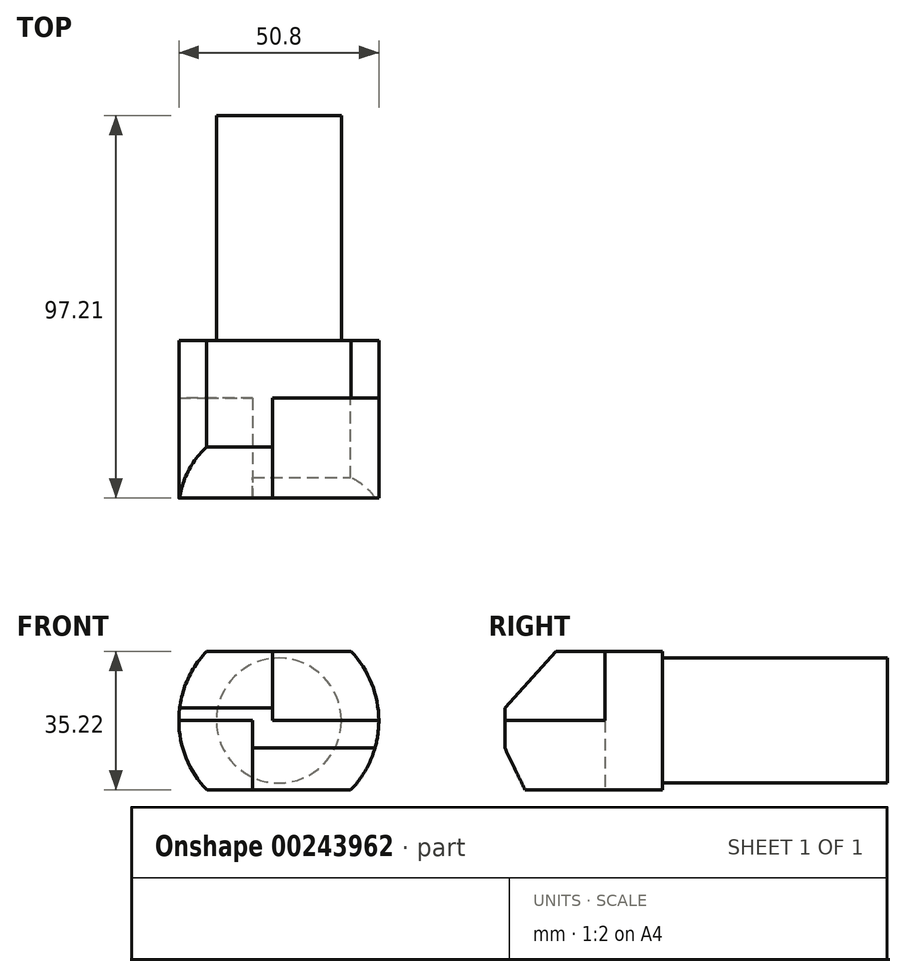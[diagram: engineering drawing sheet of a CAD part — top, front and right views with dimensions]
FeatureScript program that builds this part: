
annotation { "Feature Type Name" : "Feature", "Feature Type Description" : "" }
export const myFeature = defineFeature(function(context is Context, id is Id, definition is map)
    precondition{}
    {
        {
            var Q0;
            Q0=qCreatedBy(makeId("Front.planeOp"),FACE);
            var sketch = newSketch(context, id + "F0", { "sketchPlane" : qUnion([Q0])});
            skCircle(sketch, "E0", {"center": v(0, 0) * mm, "radius": 15.88 * mm});
            skSolve(sketch);
        }
        {
            var Q0;
            Q0 = qSketchRegion(id + "F0", true);
            extrude(context, id + "F1", {"entities" : qUnion([Q0]), "depth" : 57.15 * mm});
        }
        {
            var Q0;
            Q0=makeQuery(id+"F1.opExtrude","CAP_FACE",FACE,{"disambiguationData":[OSD([sQuery(id+"F0.wireOp",EDGE,"E0")])],"isStart":false});
            var sketch = newSketch(context, id + "F2", { "sketchPlane" : qUnion([Q0])});
            skCircle(sketch, "E1", {"center": v(0, 0) * mm, "radius": 25.4 * mm});
            skSolve(sketch);
        }
        {
            var Q0;
            Q0 = qSketchRegion(id + "F2", true);
            extrude(context, id + "F3", {"entities" : qUnion([Q0]), "operationType" : NewBodyOperationType.ADD, "depth" : 40.06 * mm});
        }
        {
            var Q0;
            Q0=makeQuery(id+"F3.opExtrude","CAP_FACE",FACE,{"disambiguationData":[OSD([sQuery(id+"F2.wireOp",EDGE,"E1")])],"isStart":false});
            var sketch = newSketch(context, id + "F4", { "sketchPlane" : qUnion([Q0])});
            skLineSegment(sketch, "E2.bottom", {"start": v(25.4, 0) * mm, "end": v(-1.6, 0) * mm});
            skLineSegment(sketch, "E2.top", {"start": v(25.4, 32.82) * mm, "end": v(-1.6, 32.82) * mm});
            skLineSegment(sketch, "E2.left", {"start": v(25.4, 0) * mm, "end": v(25.4, 32.82) * mm});
            skLineSegment(sketch, "E2.right", {"start": v(-1.6, 0) * mm, "end": v(-1.6, 32.82) * mm});
            skSolve(sketch);
        }
        {
            var Q0;
            Q0 = qSketchRegion(id + "F4", true);
            extrude(context, id + "F5", {"entities" : qUnion([Q0]), "operationType" : NewBodyOperationType.REMOVE, "oppositeDirection" : true, "depth" : 25.4 * mm});
        }
        {
            var Q0;
            Q0=makeQuery(id+"F3.opExtrude","CAP_FACE",FACE,{"disambiguationData":[OSD([sQuery(id+"F2.wireOp",EDGE,"E1")])],"isStart":false});
            var sketch = newSketch(context, id + "F6", { "sketchPlane" : qUnion([Q0])});
            skLineSegment(sketch, "E3.bottom", {"start": v(-6.65, 0) * mm, "end": v(-28.92, 0) * mm});
            skLineSegment(sketch, "E3.top", {"start": v(-6.65, -30.07) * mm, "end": v(-28.92, -30.07) * mm});
            skLineSegment(sketch, "E3.left", {"start": v(-6.65, 0) * mm, "end": v(-6.65, -30.07) * mm});
            skLineSegment(sketch, "E3.right", {"start": v(-28.92, 0) * mm, "end": v(-28.92, -30.07) * mm});
            skSolve(sketch);
        }
        {
            var Q0;
            Q0 = qSketchRegion(id + "F6", true);
            extrude(context, id + "F7", {"entities" : qUnion([Q0]), "operationType" : NewBodyOperationType.REMOVE, "oppositeDirection" : true, "depth" : 25.4 * mm});
        }
        {
            var Q0;
            Q0=qCreatedBy(makeId("Right.planeOp"),FACE);
            var sketch = newSketch(context, id + "F8", { "sketchPlane" : qUnion([Q0])});
            skLineSegment(sketch, "E4.bottom", {"start": v(-55.9, 17.55) * mm, "end": v(-109.4, 17.55) * mm});
            skLineSegment(sketch, "E4.top", {"start": v(-55.9, 32.06) * mm, "end": v(-109.4, 32.06) * mm});
            skLineSegment(sketch, "E4.left", {"start": v(-55.9, 17.55) * mm, "end": v(-55.9, 32.06) * mm});
            skLineSegment(sketch, "E4.right", {"start": v(-109.4, 17.55) * mm, "end": v(-109.4, 32.06) * mm});
            skSolve(sketch);
        }
        {
            var Q0;
            Q0 = qSketchRegion(id + "F8", true);
            extrude(context, id + "F9", {"entities" : qUnion([Q0]), "operationType" : NewBodyOperationType.REMOVE, "endBound" : BoundingType.SYMMETRIC, "oppositeDirection" : true, "depth" : 76.2 * mm});
        }
        {
            var Q0;
            Q0=makeQuery(id+"F5.boolean.opBoolean","COPY",FACE,{"derivedFrom":makeQuery(id+"F5.opExtrude","SWEPT_FACE",FACE,{"disambiguationData":[OSD([sQuery(id+"F4.wireOp",EDGE,"E2.right")])]})});
            var sketch = newSketch(context, id + "F10", { "sketchPlane" : qUnion([Q0])});
            skLineSegment(sketch, "E5", {"start": v(-100.1, 0) * mm, "end": v(-80.6, 21.55) * mm});
            skLineSegment(sketch, "E6", {"start": v(-80.6, 21.55) * mm, "end": v(-104, 21.55) * mm});
            skLineSegment(sketch, "E7", {"start": v(-104, 21.55) * mm, "end": v(-100.1, 0) * mm});
            skSolve(sketch);
        }
        {
            var Q0;
            Q0 = qSketchRegion(id + "F10", true);
            extrude(context, id + "F11", {"entities" : qUnion([Q0]), "operationType" : NewBodyOperationType.REMOVE, "oppositeDirection" : true, "depth" : 25.4 * mm});
        }
        {
            var Q0;
            Q0=makeQuery(id+"F5.boolean.opBoolean","COPY",FACE,{"derivedFrom":makeQuery(id+"F5.opExtrude","SWEPT_FACE",FACE,{"disambiguationData":[OSD([sQuery(id+"F4.wireOp",EDGE,"E2.right")])]})});
            var sketch = newSketch(context, id + "F12", { "sketchPlane" : qUnion([Q0])});
            skLineSegment(sketch, "E8.bottom", {"start": v(-54.4, -17.67) * mm, "end": v(-112.24, -17.67) * mm});
            skLineSegment(sketch, "E8.top", {"start": v(-54.4, -33.49) * mm, "end": v(-112.24, -33.49) * mm});
            skLineSegment(sketch, "E8.left", {"start": v(-54.4, -17.67) * mm, "end": v(-54.4, -33.49) * mm});
            skLineSegment(sketch, "E8.right", {"start": v(-112.24, -17.67) * mm, "end": v(-112.24, -33.49) * mm});
            skSolve(sketch);
        }
        {
            var Q0;
            Q0 = qSketchRegion(id + "F12", true);
            extrude(context, id + "F13", {"entities" : qUnion([Q0]), "operationType" : NewBodyOperationType.REMOVE, "endBound" : BoundingType.SYMMETRIC, "depth" : 76.2 * mm});
        }
        {
            var Q0;
            Q0=makeQuery(id+"F7.boolean.opBoolean","COPY",FACE,{"derivedFrom":makeQuery(id+"F7.opExtrude","SWEPT_FACE",FACE,{"disambiguationData":[OSD([sQuery(id+"F6.wireOp",EDGE,"E3.left")])]})});
            var sketch = newSketch(context, id + "F14", { "sketchPlane" : qUnion([Q0])});
            skLineSegment(sketch, "E9", {"start": v(100.54, 0) * mm, "end": v(89.92, -22.05) * mm});
            skLineSegment(sketch, "E10", {"start": v(89.92, -22.05) * mm, "end": v(101.62, -22.05) * mm});
            skLineSegment(sketch, "E11", {"start": v(101.62, -22.05) * mm, "end": v(100.54, 0) * mm});
            skSolve(sketch);
        }
        {
            var Q0;
            Q0 = qSketchRegion(id + "F14", true);
            extrude(context, id + "F15", {"entities" : qUnion([Q0]), "operationType" : NewBodyOperationType.REMOVE, "oppositeDirection" : true, "depth" : 50.8 * mm});
        }
    });
